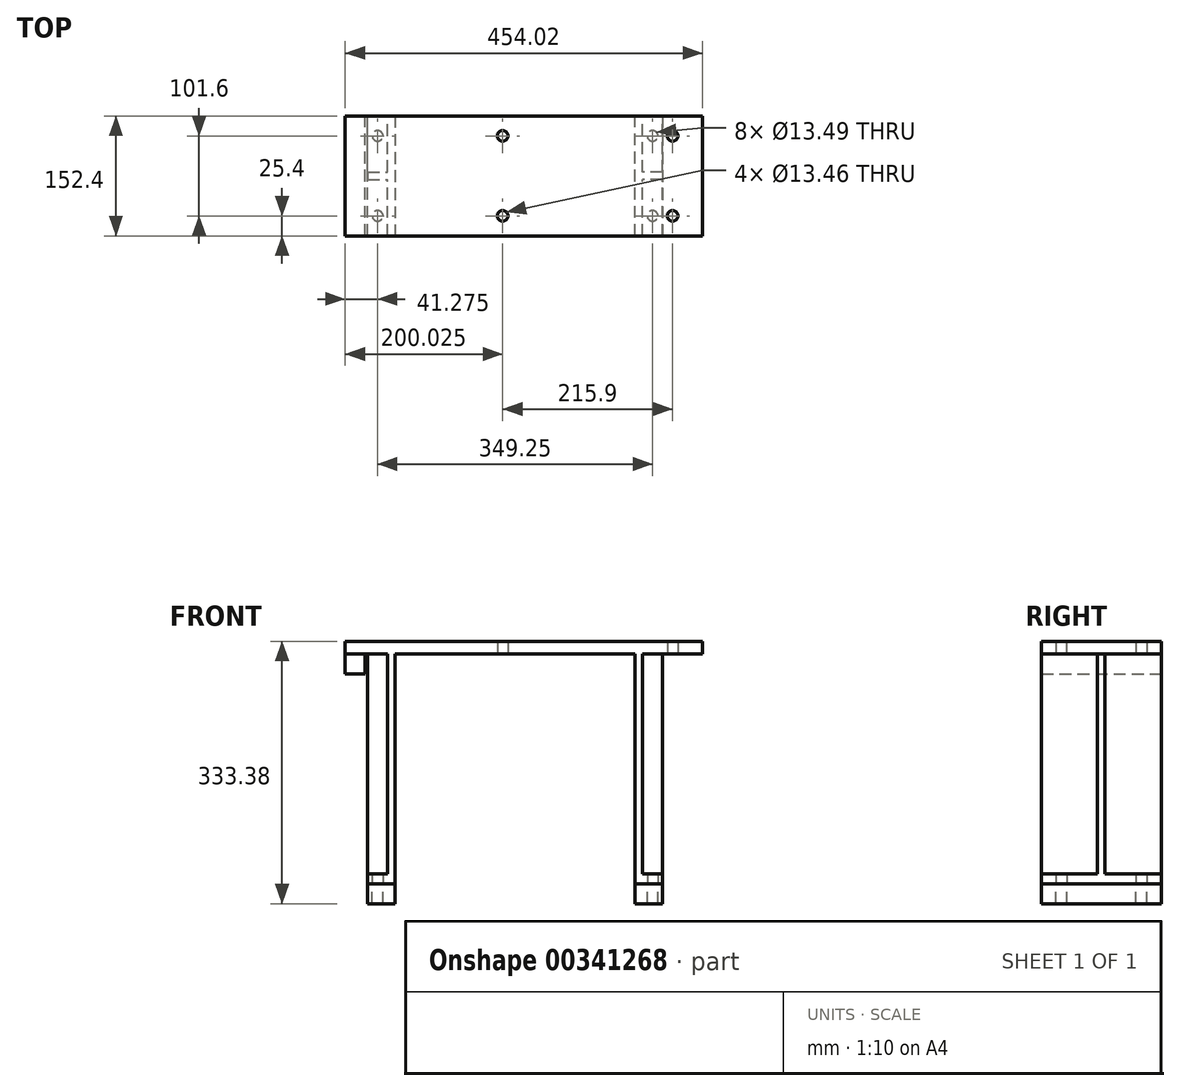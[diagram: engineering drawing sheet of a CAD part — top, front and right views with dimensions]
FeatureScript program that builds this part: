
annotation { "Feature Type Name" : "Feature", "Feature Type Description" : "" }
export const myFeature = defineFeature(function(context is Context, id is Id, definition is map)
    precondition{}
    {
        {
            var Q0;
            Q0=qCreatedBy(makeId("Top.planeOp"),FACE);
            var sketch = newSketch(context, id + "F0", { "sketchPlane" : qUnion([Q0])});
            skLineSegment(sketch, "E0", {"start": v(0, 170.24) * mm, "end": v(0, -171.77) * mm, "construction": true});
            skLineSegment(sketch, "E1", {"start": v(-339.85, 0) * mm, "end": v(353.8, 0) * mm, "construction": true});
            skLineSegment(sketch, "E2.0", {"start": v(-215.9, 170.24) * mm, "end": v(-215.9, -171.77) * mm, "construction": true});
            skLineSegment(sketch, "E3.0", {"start": v(-15.87, 170.24) * mm, "end": v(-15.87, -171.77) * mm, "construction": true});
            skLineSegment(sketch, "E4.0", {"start": v(-339.85, -76.2) * mm, "end": v(353.8, -76.2) * mm, "construction": true});
            skLineSegment(sketch, "E5.bottom", {"start": v(-215.9, -76.2) * mm, "end": v(238.13, -76.2) * mm});
            skLineSegment(sketch, "E5.top", {"start": v(-215.9, 76.2) * mm, "end": v(238.13, 76.2) * mm});
            skLineSegment(sketch, "E5.left", {"start": v(-215.9, -76.2) * mm, "end": v(-215.9, 76.2) * mm});
            skLineSegment(sketch, "E5.right", {"start": v(238.13, -76.2) * mm, "end": v(238.13, 76.2) * mm});
            skLineSegment(sketch, "E6.0", {"start": v(200.03, 170.24) * mm, "end": v(200.03, -171.77) * mm, "construction": true});
            skLineSegment(sketch, "E7.0", {"start": v(-339.85, -50.8) * mm, "end": v(353.8, -50.8) * mm, "construction": true});
            skPoint(sketch, "E8", {"position": v(-15.87, -50.8) * mm});
            skPoint(sketch, "E9", {"position": v(200.03, -50.8) * mm});
            skPoint(sketch, "E10.MirrorP", {"position": v(-15.87, 50.8) * mm});
            skPoint(sketch, "E11.MirrorP", {"position": v(200.03, 50.8) * mm});
            skCircle(sketch, "E12", {"center": v(-15.87, 50.8) * mm, "radius": 6.73 * mm});
            skCircle(sketch, "E13", {"center": v(200.03, 50.8) * mm, "radius": 6.73 * mm});
            skCircle(sketch, "E14", {"center": v(200.03, -50.8) * mm, "radius": 6.73 * mm});
            skCircle(sketch, "E15", {"center": v(-15.87, -50.8) * mm, "radius": 6.73 * mm});
            skSolve(sketch);
        }
        {
            var Q0;
            Q0=qSketchRegion(id+"F0",true);
            extrude(context, id + "F1", {"entities" : qUnion([Q0]), "depth" : 15.88 * mm});
        }
        {
            var Q0;
            Q0=makeQuery(id+"F1.opExtrude","CAP_FACE",FACE,{"disambiguationData":[OSD([sQuery(id+"F0.wireOp",EDGE,"E5.bottom"),sQuery(id+"F0.wireOp",EDGE,"E5.top"),sQuery(id+"F0.wireOp",EDGE,"E5.left"),sQuery(id+"F0.wireOp",EDGE,"E5.right"),sQuery(id+"F0.wireOp",EDGE,"E12"),sQuery(id+"F0.wireOp",EDGE,"E13"),sQuery(id+"F0.wireOp",EDGE,"E14"),sQuery(id+"F0.wireOp",EDGE,"E15")])],"isStart":true});
            var sketch = newSketch(context, id + "F2", { "sketchPlane" : qUnion([Q0])});
            skLineSegment(sketch, "E16.bottom", {"start": v(-215.9, 76.2) * mm, "end": v(-190.5, 76.2) * mm});
            skLineSegment(sketch, "E16.top", {"start": v(-215.9, -76.2) * mm, "end": v(-190.5, -76.2) * mm});
            skLineSegment(sketch, "E16.left", {"start": v(-215.9, 76.2) * mm, "end": v(-215.9, -76.2) * mm});
            skLineSegment(sketch, "E16.right", {"start": v(-190.5, 76.2) * mm, "end": v(-190.5, -76.2) * mm});
            skSolve(sketch);
        }
        {
            var Q0;
            Q0=makeQuery(id+"F2.imprint","IMPRINT",FACE,{"disambiguationData":[TD([[makeQuery(id+"F2.imprint","IMPRINT",EDGE,{"derivedFrom":sQuery(id+"F2.wireOp",EDGE,"E16.bottom")}),-1.0]])]});
            extrude(context, id + "F3", {"entities" : qUnion([Q0]), "depth" : 25.4 * mm});
        }
        {
            var Q0;
            Q0=makeQuery(id+"F1.opExtrude","CAP_FACE",FACE,{"disambiguationData":[OSD([sQuery(id+"F0.wireOp",EDGE,"E5.bottom"),sQuery(id+"F0.wireOp",EDGE,"E5.top"),sQuery(id+"F0.wireOp",EDGE,"E5.left"),sQuery(id+"F0.wireOp",EDGE,"E5.right"),sQuery(id+"F0.wireOp",EDGE,"E12"),sQuery(id+"F0.wireOp",EDGE,"E13"),sQuery(id+"F0.wireOp",EDGE,"E14"),sQuery(id+"F0.wireOp",EDGE,"E15")])],"isStart":true});
            cPlane(context, id + "F4", {"entities" : qUnion([Q0]), "cplaneType" : CPlaneType.OFFSET, "offset" : 292.1 * mm, "width" : 152.4 * mm, "height" : 152.4 * mm});
        }
        {
            var Q0;
            Q0=qCreatedBy(makeId("Right.planeOp"),FACE);
            cPlane(context, id + "F5", {"entities" : qUnion([Q0]), "cplaneType" : CPlaneType.OFFSET, "offset" : 152.4 * mm, "width" : 152.4 * mm, "height" : 152.4 * mm});
        }
        {
            var Q0;
            Q0=qCreatedBy(id+"F5.planeOp",FACE);
            var sketch = newSketch(context, id + "F6", { "sketchPlane" : qUnion([Q0])});
            skLineSegment(sketch, "E17.0", {"start": v(-76.2, -25.4) * mm, "end": v(76.2, -25.4) * mm, "construction": true});
            skLineSegment(sketch, "E18.0", {"start": v(-76.2, 0) * mm, "end": v(76.2, 0) * mm, "construction": true});
            skLineSegment(sketch, "E19.bottom", {"start": v(76.2, 0) * mm, "end": v(-76.2, 0) * mm});
            skLineSegment(sketch, "E19.top", {"start": v(76.2, -292.1) * mm, "end": v(-76.2, -292.1) * mm});
            skLineSegment(sketch, "E19.left", {"start": v(76.2, 0) * mm, "end": v(76.2, -292.1) * mm});
            skLineSegment(sketch, "E19.right", {"start": v(-76.2, 0) * mm, "end": v(-76.2, -292.1) * mm});
            skSolve(sketch);
        }
        {
            var Q0;
            Q0=makeQuery(id+"F6.imprint","IMPRINT",FACE,{"disambiguationData":[TD([[makeQuery(id+"F6.imprint","IMPRINT",EDGE,{"derivedFrom":sQuery(id+"F6.wireOp",EDGE,"E19.bottom")}),1.0]])]});
            extrude(context, id + "F7", {"entities" : qUnion([Q0]), "depth" : 9.52 * mm});
        }
        {
            var Q0;
            Q0=qCreatedBy(id+"F4.planeOp",FACE);
            var sketch = newSketch(context, id + "F8", { "sketchPlane" : qUnion([Q0])});
            skLineSegment(sketch, "E20.0", {"start": v(161.93, -76.2) * mm, "end": v(161.93, 76.2) * mm, "construction": true});
            skLineSegment(sketch, "E21.0", {"start": v(187.33, -76.2) * mm, "end": v(187.33, 76.2) * mm, "construction": true});
            skLineSegment(sketch, "E22.0", {"start": v(152.4, -76.2) * mm, "end": v(152.4, 76.2) * mm, "construction": true});
            skLineSegment(sketch, "E23.bottom", {"start": v(152.4, 76.2) * mm, "end": v(187.33, 76.2) * mm});
            skLineSegment(sketch, "E23.top", {"start": v(152.4, -76.2) * mm, "end": v(187.33, -76.2) * mm});
            skLineSegment(sketch, "E23.left", {"start": v(152.4, 76.2) * mm, "end": v(152.4, -76.2) * mm});
            skLineSegment(sketch, "E23.right", {"start": v(187.33, 76.2) * mm, "end": v(187.33, -76.2) * mm});
            skSolve(sketch);
        }
        {
            var Q0;
            Q0=qSketchRegion(id+"F8",true);
            extrude(context, id + "F9", {"entities" : qUnion([Q0]), "operationType" : NewBodyOperationType.ADD, "oppositeDirection" : true, "depth" : 12.7 * mm});
        }
        {
            var Q0;
            Q0=makeQuery(id+"F9.boolean.opBoolean","MERGE",FACE,{"derivedFrom":[makeQuery(id+"F7.opExtrude","SWEPT_FACE",FACE,{"disambiguationData":[OSD([sQuery(id+"F6.wireOp",EDGE,"E19.top")])]}),makeQuery(id+"F9.opExtrude","CAP_FACE",FACE,{"disambiguationData":[OSD([sQuery(id+"F8.wireOp",EDGE,"E23.bottom"),sQuery(id+"F8.wireOp",EDGE,"E23.top"),sQuery(id+"F8.wireOp",EDGE,"E23.left"),sQuery(id+"F8.wireOp",EDGE,"E23.right")])],"isStart":true})]});
            var sketch = newSketch(context, id + "F10", { "sketchPlane" : qUnion([Q0])});
            skLineSegment(sketch, "E24.0", {"start": v(187.33, 76.2) * mm, "end": v(187.33, -76.2) * mm, "construction": true});
            skLineSegment(sketch, "E25.0", {"start": v(174.63, 76.2) * mm, "end": v(174.63, -76.2) * mm, "construction": true});
            skLineSegment(sketch, "E26", {"start": v(261.95, 0) * mm, "end": v(121.14, 0) * mm, "construction": true});
            skPoint(sketch, "E26.startSnap0", {"position": v(187.33, 0) * mm});
            skPoint(sketch, "E26.endSnap0", {"position": v(187.33, 0) * mm});
            skLineSegment(sketch, "E27.0", {"start": v(261.95, 50.8) * mm, "end": v(121.14, 50.8) * mm, "construction": true});
            skPoint(sketch, "E28", {"position": v(174.63, 50.8) * mm});
            skPoint(sketch, "E29.MirrorP", {"position": v(174.63, -50.8) * mm});
            skSolve(sketch);
        }
        {
            var Q0;
            Q0=sQuery(id+"F10.wireOp",VERTEX,"E28");
            var Q1;
            Q1=sQuery(id+"F10.wireOp",VERTEX,"E29.MirrorP");
            var Q2;
            Q2=makeQuery(id+"F7.opExtrude","SWEPT_BODY",BODY,{"disambiguationData":[OSD([sQuery(id+"F6.wireOp",EDGE,"E19.bottom"),sQuery(id+"F6.wireOp",EDGE,"E19.top"),sQuery(id+"F6.wireOp",EDGE,"E19.left"),sQuery(id+"F6.wireOp",EDGE,"E19.right")])]});
            hole(context, id + "F11", {"style" : HoleStyle.SIMPLE, "endStyle" : HoleEndStyle.BLIND, "standardTappedOrClearance" : lookupTablePath({ "standard" : "ANSI", "fit" : "Normal (ASME)", "size" : "1/2", "type" : "Clearance" }), "standardBlindInLast" : lookupTablePath({ "fit" : "Free", "standard" : "ANSI", "size" : "1/2", "type" : "Clearance" }), "holeDiameter" : 13.5 * mm, "holeDepth" : 25.4 * mm, "tappedDepth" : 19.53 * mm, "tapClearance" : 3, "locations" : qUnion([Q0, Q1]), "scope" : qUnion([Q2])});
        }
        {
            var Q0;
            Q0=makeQuery(id+"F7.opExtrude","SWEPT_BODY",BODY,{"disambiguationData":[OSD([sQuery(id+"F6.wireOp",EDGE,"E19.bottom"),sQuery(id+"F6.wireOp",EDGE,"E19.top"),sQuery(id+"F6.wireOp",EDGE,"E19.left"),sQuery(id+"F6.wireOp",EDGE,"E19.right")])]});
            var Q1;
            Q1=qCreatedBy(makeId("Right.planeOp"),FACE);
            mirror(context, id + "F12", {"operationType" : NewBodyOperationType.ADD, "entities" : qUnion([Q0]), "mirrorPlane" : qUnion([Q1])});
        }
        {
            var Q0;
            Q0=makeQuery(id+"F12.opPattern","COPY",FACE,{"derivedFrom":makeQuery(id+"F7.opExtrude","CAP_FACE",FACE,{"disambiguationData":[OSD([sQuery(id+"F6.wireOp",EDGE,"E19.bottom"),sQuery(id+"F6.wireOp",EDGE,"E19.top"),sQuery(id+"F6.wireOp",EDGE,"E19.left"),sQuery(id+"F6.wireOp",EDGE,"E19.right")])],"isStart":false}),"instanceName":"1"});
            var sketch = newSketch(context, id + "F13", { "sketchPlane" : qUnion([Q0])});
            skLineSegment(sketch, "E30", {"start": v(0, 105.63) * mm, "end": v(0, -367.61) * mm, "construction": true});
            skLineSegment(sketch, "E31.0", {"start": v(-4.76, 105.63) * mm, "end": v(-4.76, -367.61) * mm, "construction": true});
            skLineSegment(sketch, "E32.0", {"start": v(76.2, 0) * mm, "end": v(-76.2, 0) * mm, "construction": true});
            skLineSegment(sketch, "E33.0", {"start": v(76.2, -279.4) * mm, "end": v(-76.2, -279.4) * mm, "construction": true});
            skLineSegment(sketch, "E34.bottom", {"start": v(-4.76, -279.4) * mm, "end": v(4.76, -279.4) * mm});
            skLineSegment(sketch, "E34.top", {"start": v(-4.76, 0) * mm, "end": v(4.76, 0) * mm});
            skLineSegment(sketch, "E34.left", {"start": v(-4.76, -279.4) * mm, "end": v(-4.76, 0) * mm});
            skLineSegment(sketch, "E34.right", {"start": v(4.76, -279.4) * mm, "end": v(4.76, 0) * mm});
            skSolve(sketch);
        }
        {
            var Q0;
            Q0=qSketchRegion(id+"F13",true);
            extrude(context, id + "F14", {"entities" : qUnion([Q0]), "depth" : 25.4 * mm});
        }
        {
            var Q0;
            Q0=makeQuery(id+"F14.opExtrude","SWEPT_BODY",BODY,{"disambiguationData":[OSD([sQuery(id+"F13.wireOp",EDGE,"E34.bottom"),sQuery(id+"F13.wireOp",EDGE,"E34.top"),sQuery(id+"F13.wireOp",EDGE,"E34.left"),sQuery(id+"F13.wireOp",EDGE,"E34.right")])]});
            var Q1;
            Q1=qCreatedBy(makeId("Right.planeOp"),FACE);
            mirror(context, id + "F15", {"operationType" : NewBodyOperationType.ADD, "entities" : qUnion([Q0]), "mirrorPlane" : qUnion([Q1])});
        }
        {
            var Q0;
            Q0=makeQuery(id+"F12.opPattern","COPY",FACE,{"derivedFrom":makeQuery(id+"F9.boolean.opBoolean","MERGE",FACE,{"derivedFrom":[makeQuery(id+"F7.opExtrude","SWEPT_FACE",FACE,{"disambiguationData":[OSD([sQuery(id+"F6.wireOp",EDGE,"E19.top")])]}),makeQuery(id+"F9.opExtrude","CAP_FACE",FACE,{"disambiguationData":[OSD([sQuery(id+"F8.wireOp",EDGE,"E23.bottom"),sQuery(id+"F8.wireOp",EDGE,"E23.top"),sQuery(id+"F8.wireOp",EDGE,"E23.left"),sQuery(id+"F8.wireOp",EDGE,"E23.right")])],"isStart":true})]}),"instanceName":"1"});
            var sketch = newSketch(context, id + "F16", { "sketchPlane" : qUnion([Q0])});
            skLineSegment(sketch, "E35.0.0", {"start": v(-152.4, -76.2) * mm, "end": v(-152.4, 76.2) * mm});
            skLineSegment(sketch, "E35.0.1", {"start": v(-152.4, 76.2) * mm, "end": v(-187.33, 76.2) * mm});
            skLineSegment(sketch, "E35.0.2", {"start": v(-187.33, 76.2) * mm, "end": v(-187.33, -76.2) * mm});
            skLineSegment(sketch, "E35.0.3", {"start": v(-187.33, -76.2) * mm, "end": v(-152.4, -76.2) * mm});
            skCircle(sketch, "E36.0", {"center": v(-174.63, 50.8) * mm, "radius": 6.75 * mm});
            skCircle(sketch, "E37.0", {"center": v(-174.63, -50.8) * mm, "radius": 6.75 * mm});
            skLineSegment(sketch, "E38.0.0", {"start": v(152.4, 76.2) * mm, "end": v(152.4, -76.2) * mm});
            skLineSegment(sketch, "E38.0.1", {"start": v(152.4, -76.2) * mm, "end": v(187.33, -76.2) * mm});
            skLineSegment(sketch, "E38.0.2", {"start": v(187.33, -76.2) * mm, "end": v(187.33, 76.2) * mm});
            skLineSegment(sketch, "E38.0.3", {"start": v(187.33, 76.2) * mm, "end": v(152.4, 76.2) * mm});
            skCircle(sketch, "E39.0", {"center": v(174.63, -50.8) * mm, "radius": 6.75 * mm});
            skCircle(sketch, "E40.0", {"center": v(174.63, 50.8) * mm, "radius": 6.75 * mm});
            skSolve(sketch);
        }
        {
            var Q0;
            Q0=qSketchRegion(id+"F16",true);
            extrude(context, id + "F17", {"entities" : qUnion([Q0]), "depth" : 25.4 * mm});
        }
    });
